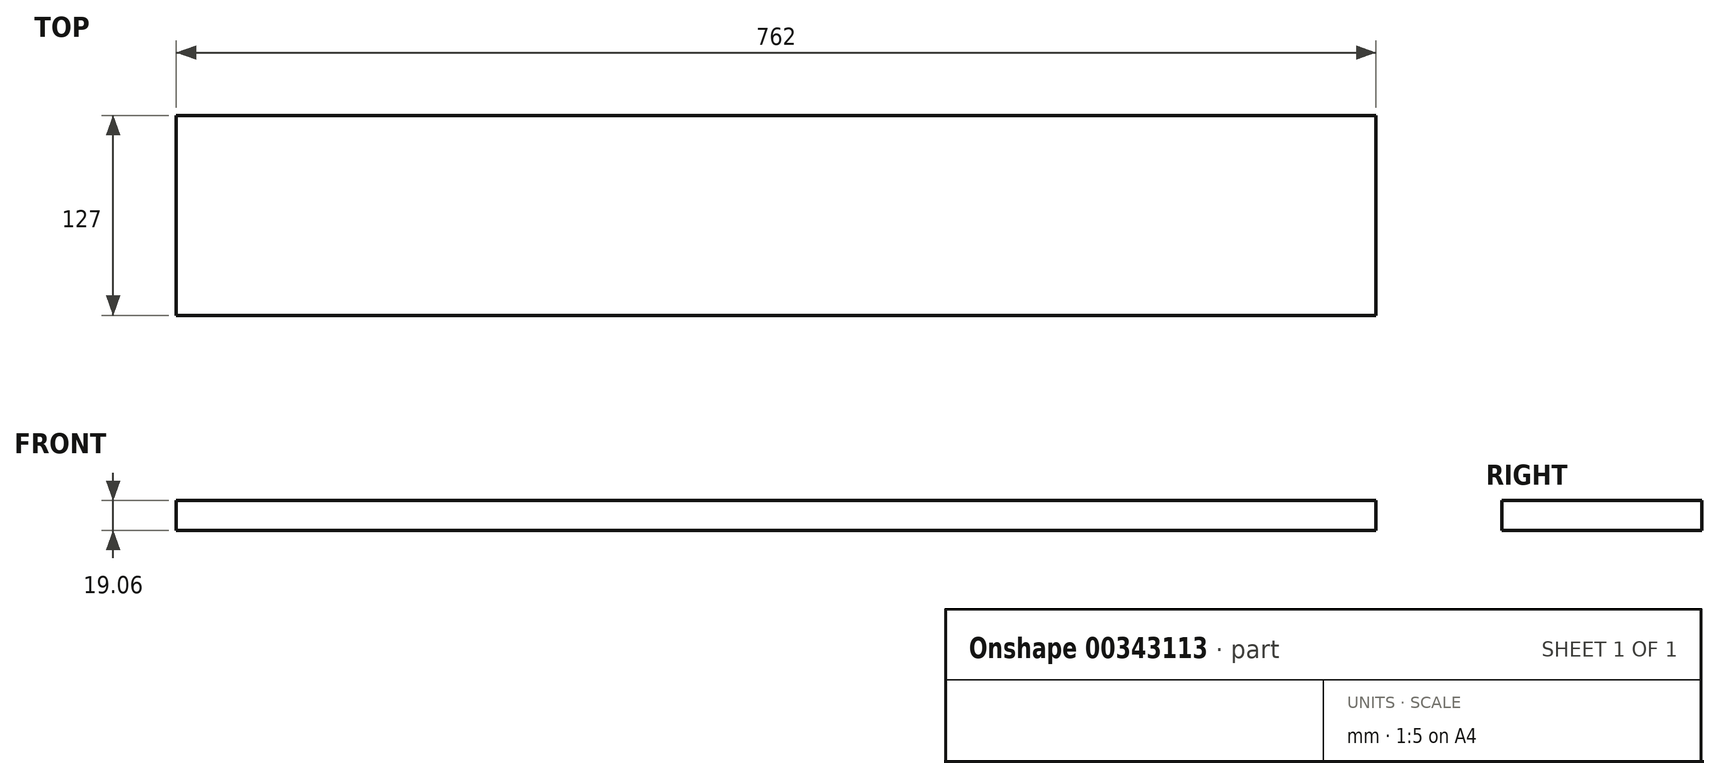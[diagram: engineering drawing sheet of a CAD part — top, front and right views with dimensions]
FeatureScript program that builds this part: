
annotation { "Feature Type Name" : "Feature", "Feature Type Description" : "" }
export const myFeature = defineFeature(function(context is Context, id is Id, definition is map)
    precondition{}
    {
        {
            var Q0;
            Q0=qCreatedBy(makeId("Right.planeOp"),FACE);
            var sketch = newSketch(context, id + "F0", { "sketchPlane" : qUnion([Q0])});
            skLineSegment(sketch, "E0.bottom", {"start": v(-63.5, 9.53) * mm, "end": v(63.5, 9.53) * mm});
            skLineSegment(sketch, "E0.top", {"start": v(-63.5, -9.52) * mm, "end": v(63.5, -9.52) * mm});
            skLineSegment(sketch, "E0.left", {"start": v(-63.5, 9.53) * mm, "end": v(-63.5, -9.52) * mm});
            skLineSegment(sketch, "E0.right", {"start": v(63.5, 9.53) * mm, "end": v(63.5, -9.52) * mm});
            skSolve(sketch);
        }
        {
            var Q0;
            Q0=makeQuery(id+"F0.imprint","IMPRINT",FACE,{"disambiguationData":[TD([[makeQuery(id+"F0.imprint","IMPRINT",EDGE,{"derivedFrom":sQuery(id+"F0.wireOp",EDGE,"E0.bottom")}),-1.0]])]});
            extrude(context, id + "F1", {"entities" : qUnion([Q0]), "endBound" : BoundingType.SYMMETRIC, "depth" : 762 * mm});
        }
    });
